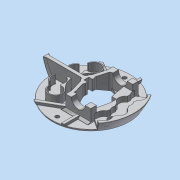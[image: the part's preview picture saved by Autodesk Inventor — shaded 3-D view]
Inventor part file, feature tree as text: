
AUTODESK INVENTOR PART (.ipt)
format: ipt  version: 2017 (Build 210142000, 142)  size: 2,428,928 bytes
history: native  units: mm
features: fillet x36, projected_geometry x31, sketch x29, extrude x20, plane x8, hole x7, mirror x4, revolve x3, other x3, loft x2, chamfer x2, pattern_circular x1
ambient origin geometry x8: Origin, YZ Plane, XZ Plane, XY Plane, X Axis, Y Axis, Z Axis, Center Point
bodies: Volumenkörper1 (feature_tree)
feature tree (146):
  revolve  "Umdrehung1"
  sketch  "Skizze6"  dims[d7=5.0mm d8=90.0deg]
  plane  "Arbeitsebene2"
  sketch  "Skizze7"  dims[d28=0.25mm d36=4.0mm]
  plane  "Arbeitsebene3"
  sketch  "Skizze8"  dims[d38=2.0mm d40=1.2mm]
  loft  "Erhebung1"
  extrude  "Extrusion16"  TaperAngle=90.0deg  [1 undecoded]
  other  "Rippe1"
  extrude  "Extrusion17"  Depth=4.0mm
  extrude  "Extrusion21"  Depth=1.2mm
  hole  "Bohrung4"  [1 undecoded]
  hole  "Bohrung3"  [1 undecoded]
  plane  "Arbeitsebene11"
  mirror  "Spiegeln6"
  mirror  "Spiegeln3"
  extrude  "Extrusion18"  TaperAngle=0.0deg  [1 undecoded]
  extrude  "Extrusion20"  TaperAngle=60.0deg  [1 undecoded]
  sketch  "Skizze37"  dims[d63=2.5mm d64=1.0mm d65=0.0mm d66=0.0mm d67=1.0mm d68=1.0mm d82=51.0mm]
  extrude  "Extrusion19"  Depth=51.0mm
  extrude  "Extrusion22"  Depth=53.0mm
  plane  "Arbeitsebene13"
  extrude  "Extrusion23"  Depth=1.0mm
  extrude  "Extrusion24"  Depth=8.0mm
  chamfer  "Fase3"  Distance=10.0mm
  chamfer  "Fase2"  Distance=10.0mm
  mirror  "Spiegeln8"
  plane  "Arbeitsebene14"
  plane  "Arbeitsebene1"
  hole  "Bohrung1"  [1 undecoded]
  fillet  "Rundung2"  Radius=17.348736mm
  extrude  "Extrusion29"  TaperAngle=90.0deg  [1 undecoded]
  extrude  "Extrusion28"  Depth=5.25mm
  extrude  "Extrusion31"  Depth=3.490659mm
  loft  "Erhebung3"
  sketch  "Skizze57"  dims[d184=2.459mm d185=6.0mm d186=4.0mm d187=2.0mm d188=90.0deg d189=8.8mm d190=20.594885mm d191=6.0mm d194=17.348736mm]
  plane  "Arbeitsebene16"
  extrude  "Extrusion32"  Depth=7.0mm TaperAngle=0.0deg
  sketch  "Skizze61"  dims[d206=90.0deg d207=5.25mm]
  extrude  "Extrusion34"  TaperAngle=90.0deg  [1 undecoded]
  hole  "Bohrung5"  [1 undecoded]
  pattern_circular  "Runde Anordnung1"  [2 undecoded]
  revolve  "Umdrehung9"
  revolve  "Umdrehung10"
  extrude  "Extrusion35"  Depth=0.2mm
  extrude  "Extrusion36"  Depth=0.2mm
  fillet  "Rundung5"  Radius=15.0mm
  extrude  "Extrusion37"  Depth=0.2mm
  extrude  "Extrusion38"  Depth=0.2mm
  fillet  "Rundung6"  Radius=5.0mm
  fillet  "Rundung8"  Radius=15.0mm
  fillet  "Rundung9"  Radius=2.0mm
  fillet  "Rundung10"  Radius=1.0mm
  fillet  "Rundung11"  Radius=1.5mm
  fillet  "Rundung12"  Radius=9.699mm
  fillet  "Rundung13"  [1 undecoded]
  fillet  "Rundung14"  Radius=1.0mm
  fillet  "Rundung15"  Radius=0.8mm
  fillet  "Rundung17"  Radius=10.0mm
  fillet  "Rundung18"  Radius=6.0mm
  fillet  "Rundung19"  Radius=37.5mm
  fillet  "Rundung20"  Radius=13.919411mm
  fillet  "Rundung21"  Radius=8.905149mm
  fillet  "Rundung22"  Radius=27.925268mm
  fillet  "Rundung24"  Radius=37.5mm
  fillet  "Rundung25"  Radius=8.905149mm
  fillet  "Rundung26"  [1 undecoded]
  fillet  "Rundung27"  Radius=17.0mm
  fillet  "Rundung28"  Radius=10.0mm
  fillet  "Rundung29"  Radius=22.0mm
  fillet  "Rundung30"  Radius=5.0mm
  fillet  "Rundung31"  Radius=17.0mm
  fillet  "Rundung32"  [1 undecoded]
  fillet  "Rundung34"  [1 undecoded]
  fillet  "Rundung35"  Radius=10.5mm
  fillet  "Rundung36"  [1 undecoded]
  fillet  "Rundung39"  Radius=8.0mm
  hole  "Bohrung6"  [1 undecoded]
  hole  "Bohrung7"  [1 undecoded]
  hole  "Bohrung8"  [1 undecoded]
  fillet  "Rundung40"  Radius=4.5mm
  extrude  "Extrusion39"  Depth=0.2mm
  fillet  "Rundung41"  Radius=5.0mm
  fillet  "Rundung42"  [1 undecoded]
  fillet  "Rundung43"  Radius=5.5mm
  fillet  "Rundung44"  [1 undecoded]
  extrude  "Extrusion40"  Depth=0.2mm
  plane  "Arbeitsebene17"
  mirror  "Spiegeln10"
  fillet  "Rundung45"  Radius=2.5mm
  sketch  "Skizze1"  dims[d3=5.0mm d5=50.0mm]
  projected_geometry  "Projizierte Kontur1"
  sketch  "Skizze9"  dims[d41=45.0mm d49=4.0mm]
  projected_geometry  "Projizierte Kontur3"
  projected_geometry  "Projizierte Kontur4"
  projected_geometry  "Projizierte Kontur5"
  projected_geometry  "Projizierte Kontur6"
  sketch  "Skizze13"  dims[d50=22.0mm d51=5.0mm]
  projected_geometry  "Projizierte Kontur10"
  sketch  "Skizze31"  dims[d53=10.0mm d54=0.0mm d55=90.0deg]
  sketch  "Skizze32"  dims[d56=0.0mm d57=90.0deg d62=60.0deg]
  projected_geometry  "Projizierte Kontur20"
  projected_geometry  "Projizierte Kontur22"
  projected_geometry  "Projizierte Kontur23"
  sketch  "Skizze39"  dims[d83=45.0mm d84=53.0mm]
  projected_geometry  "Projizierte Kontur24"
  projected_geometry  "Projizierte Kontur25"
  projected_geometry  "Projizierte Kontur28"
  projected_geometry  "Projizierte Kontur29"
  sketch  "Skizze44"  dims[d85=60.0mm d87=360.0deg]
  projected_geometry  "Projizierte Kontur31"
  sketch  "Skizze46"  dims[d89=2.459mm d90=6.0mm d91=4.0mm d92=2.0mm d93=90.0deg d94=5.0mm d95=20.594885mm d97=1.0mm d98=25.0mm]
  projected_geometry  "Projizierte Kontur41"
  projected_geometry  "Projizierte Kontur42"
  projected_geometry  "Projizierte Kontur43"
  projected_geometry  "Projizierte Kontur49"
  sketch  "Skizze53"  dims[d99=8.0mm d130=8.0mm d176=10.0mm d177=0.0mm]
  sketch  "Skizze54"  dims[d179=3.0mm]
  sketch  "Skizze55"  dims[d180=25.0mm]
  sketch  "Skizze56"  dims[d181=12.0mm d182=10.0mm d183=0.0mm]
  projected_geometry  "Projizierte Kontur50"
  projected_geometry  "Projizierte Kontur51"
  sketch  "Skizze60"  dims[d201=9.0mm d202=0.0mm d203=90.0deg]
  sketch  "Skizze62"  dims[d208=90.0deg d209=3.490659mm]
  sketch  "Skizze64"  dims[d210=90.0deg d211=10.5mm]
  sketch  "Skizze65"  dims[d214=1.0mm d215=7.0mm d216=0.0mm]
  projected_geometry  "Projizierte Kontur54"
  sketch  "Skizze66"  dims[d218=120.0deg d220=90.0deg]
  sketch  "Skizze67"  dims[d222=10.0mm d223=0.0mm d224=60.0deg]
  projected_geometry  "Projizierte Kontur55"
  sketch  "Skizze68"  dims[d225=5.0mm]
  sketch  "Skizze69"  dims[d227=7.0mm d228=0.0mm]
  projected_geometry  "Projizierte Kontur56"
  projected_geometry  "Projizierte Kontur57"
  sketch  "Skizze70"  dims[d235=2.4mm d236=6.0mm d237=3.0mm d238=2.0mm d239=90.0deg d240=5.0mm d241=20.594885mm]
  projected_geometry  "Projizierte Kontur58"
  projected_geometry  "Projizierte Kontur59"
  sketch  "Skizze73"  dims[d242=7.0mm d243=0.0mm]
  projected_geometry  "Projizierte Kontur60"
  sketch  "Skizze74"  dims[d244=5.0mm d245=2.0mm d246=4.0mm d247=3.0mm d248=15.0mm d249=0.0mm d252=3.0mm d253=1.0mm d255=5.0mm d257=15.0mm d258=0.0mm d259=2.0mm d262=11.0mm d263=5.0mm d264=45.0deg d266=1.0mm d268=1.5mm d269=9.699mm d270=5.0mm d271=45.0deg d272=0.0mm d276=1.0mm d277=0.8mm d292=10.0mm d293=6.0mm d294=37.5mm d295=13.919411mm d296=8.905149mm d297=27.925268mm d298=37.5mm d302=8.905149mm d303=0.0mm d304=17.0mm d305=10.0mm d306=0.0mm d310=22.0mm d311=5.0mm d312=0.0mm d313=17.0mm d314=0.0mm d315=90.0deg d316=0.0mm d317=90.0deg d318=10.5mm d325=0.0mm d326=8.0mm d327=4.363323mm d328=3.2mm d329=4.5mm d330=4.5mm d331=3.2mm d332=5.0mm d333=0.0mm d334=5.5mm d335=120.0deg d336=2.38157mm d339=2.5mm d340=0.0mm d341=3.2mm d342=6.0mm d343=4.0mm d344=2.0mm d345=90.0deg d346=8.0mm d347=20.594885mm d348=60.0mm d349=360.0deg d351=90.0deg d352=2.0mm d353=90.0deg d354=10.5mm d355=10.5mm d356=10.5mm d357=10.5mm d358=4.5mm d359=0.0mm d361=8.0mm d362=7.0mm d363=10.0mm d364=0.0mm d372=1.0mm d373=10.0mm d374=0.0mm d375=10.0mm d376=0.0mm d381=7.0mm d382=0.2mm d384=0.2mm d385=0.2mm d386=0.2mm d387=0.2mm d388=0.2mm d389=0.2mm d390=0.2mm d391=0.2mm d393=0.2mm d394=0.2mm d395=0.2mm d396=0.2mm d397=0.2mm d398=7.0mm d399=0.2mm d401=0.2mm d402=0.2mm d403=0.2mm d404=0.2mm d405=0.2mm d406=0.2mm d407=0.2mm d408=0.2mm d409=0.2mm d411=0.2mm d412=0.2mm d413=0.2mm d416=0.1mm d417=29.0mm d418=29.0mm d419=3.0mm d420=6.0mm d421=4.0mm d422=2.0mm d423=90.0deg d424=8.0mm d425=20.594885mm d426=3.0mm d427=6.0mm d428=4.0mm d429=2.0mm d430=90.0deg d431=8.0mm d432=20.594885mm d439=3.0mm d440=6.0mm d441=4.0mm d442=2.0mm d443=90.0deg d444=8.0mm d445=20.594885mm d449=0.2mm d455=5.7mm d456=3.5mm d457=0.0mm d458=0.2mm d459=0.2mm d460=0.2mm d461=0.2mm d462=7.0mm d463=0.0mm d464=9.5mm d465=2.0mm d466=2.5mm d467=0.2mm]
  projected_geometry  "Projizierte Kontur61"
  projected_geometry  "Projizierte Kontur62"
  projected_geometry  "Projizierte Kontur63"
  projected_geometry  "Projizierte Kontur64"
  other  "Schnittkanten projizieren1"
  other  "Schnittkanten projizieren2"
note: 21 required parameter values undecoded (feature->parameter linkage not recoverable at this tier; creation-order binding heuristic only, values carry confidence <= 0.55)
